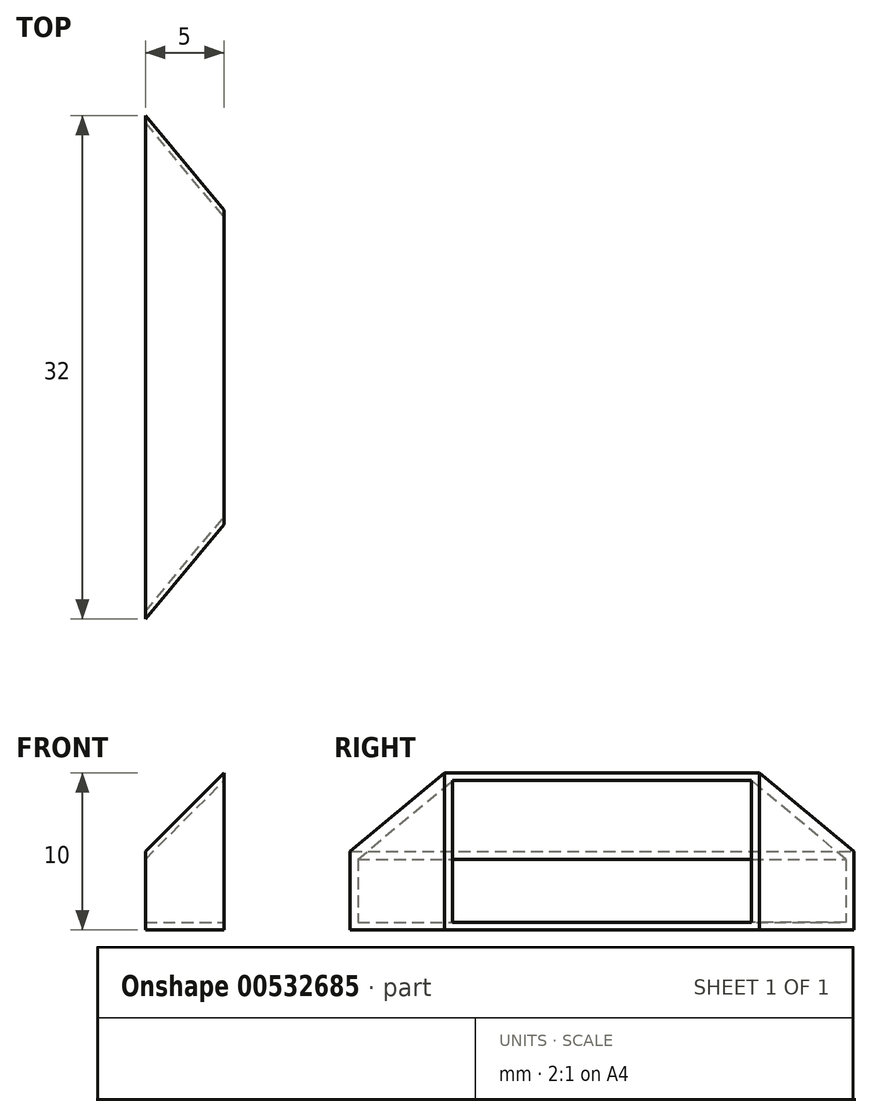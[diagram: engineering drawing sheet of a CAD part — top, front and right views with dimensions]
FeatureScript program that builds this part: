
annotation { "Feature Type Name" : "Feature", "Feature Type Description" : "" }
export const myFeature = defineFeature(function(context is Context, id is Id, definition is map)
    precondition{}
    {
        {
            var Q0;
            Q0=qCreatedBy(makeId("Right.planeOp"),FACE);
            var sketch = newSketch(context, id + "F0", { "sketchPlane" : qUnion([Q0])});
            skLineSegment(sketch, "E0.bottom", {"start": v(-16, 5) * mm, "end": v(16, 5) * mm});
            skLineSegment(sketch, "E0.top", {"start": v(-16, 0) * mm, "end": v(16, 0) * mm});
            skLineSegment(sketch, "E0.left", {"start": v(-16, 5) * mm, "end": v(-16, 0) * mm});
            skLineSegment(sketch, "E0.right", {"start": v(16, 5) * mm, "end": v(16, 0) * mm});
            skSolve(sketch);
        }
        {
            var Q0;
            Q0=qCreatedBy(makeId("Right.planeOp"),FACE);
            cPlane(context, id + "F1", {"entities" : qUnion([Q0]), "cplaneType" : CPlaneType.OFFSET, "offset" : 5 * mm, "width" : 150 * mm, "height" : 150 * mm});
        }
        {
            var Q0;
            Q0=qCreatedBy(id+"F1.planeOp",FACE);
            var sketch = newSketch(context, id + "F2", { "sketchPlane" : qUnion([Q0])});
            skLineSegment(sketch, "E1.bottom", {"start": v(-10, 10) * mm, "end": v(10, 10) * mm});
            skLineSegment(sketch, "E1.top", {"start": v(-10, 0) * mm, "end": v(10, 0) * mm});
            skLineSegment(sketch, "E1.left", {"start": v(-10, 10) * mm, "end": v(-10, 0) * mm});
            skLineSegment(sketch, "E1.right", {"start": v(10, 10) * mm, "end": v(10, 0) * mm});
            skSolve(sketch);
        }
        {
            var Q0;
            Q0=makeQuery(id+"F0.imprint","IMPRINT",FACE,{"disambiguationData":[TD([[makeQuery(id+"F0.imprint","IMPRINT",EDGE,{"derivedFrom":sQuery(id+"F0.wireOp",EDGE,"E0.bottom")}),-1.0]])]});
            var Q1;
            Q1=makeQuery(id+"F2.imprint","IMPRINT",FACE,{"disambiguationData":[TD([[makeQuery(id+"F2.imprint","IMPRINT",EDGE,{"derivedFrom":sQuery(id+"F2.wireOp",EDGE,"E1.bottom")}),-1.0]])]});
            loft(context, id + "F3", {"sheetProfilesArray" : [{ "sheetProfileEntities" : qUnion([Q0]) }, { "sheetProfileEntities" : qUnion([Q1]) }]});
        }
        {
            var Q0;
            Q0=qCreatedBy(makeId("Right.planeOp"),FACE);
            var sketch = newSketch(context, id + "F4", { "sketchPlane" : qUnion([Q0])});
            skLineSegment(sketch, "E2.bottom", {"start": v(-15.5, 4.5) * mm, "end": v(15.5, 4.5) * mm});
            skLineSegment(sketch, "E2.top", {"start": v(-15.5, 0.5) * mm, "end": v(15.5, 0.5) * mm});
            skLineSegment(sketch, "E2.left", {"start": v(-15.5, 4.5) * mm, "end": v(-15.5, 0.5) * mm});
            skLineSegment(sketch, "E2.right", {"start": v(15.5, 4.5) * mm, "end": v(15.5, 0.5) * mm});
            skSolve(sketch);
        }
        {
            var Q0;
            Q0=qCreatedBy(id+"F1.planeOp",FACE);
            var sketch = newSketch(context, id + "F5", { "sketchPlane" : qUnion([Q0])});
            skLineSegment(sketch, "E3.bottom", {"start": v(-9.5, 9.5) * mm, "end": v(9.5, 9.5) * mm});
            skLineSegment(sketch, "E3.top", {"start": v(-9.5, 0.5) * mm, "end": v(9.5, 0.5) * mm});
            skLineSegment(sketch, "E3.left", {"start": v(-9.5, 9.5) * mm, "end": v(-9.5, 0.5) * mm});
            skLineSegment(sketch, "E3.right", {"start": v(9.5, 9.5) * mm, "end": v(9.5, 0.5) * mm});
            skSolve(sketch);
        }
        {
            var Q1;
            Q1 = qSketchRegion(id + "F4", true);
            var Q2;
            Q2 = qSketchRegion(id + "F5", true);
            loft(context, id + "F6", {"operationType" : NewBodyOperationType.REMOVE, "sheetProfilesArray" : [{ "sheetProfileEntities" : qUnion([Q1]) }, { "sheetProfileEntities" : qUnion([Q2]) }]});
        }
    });
